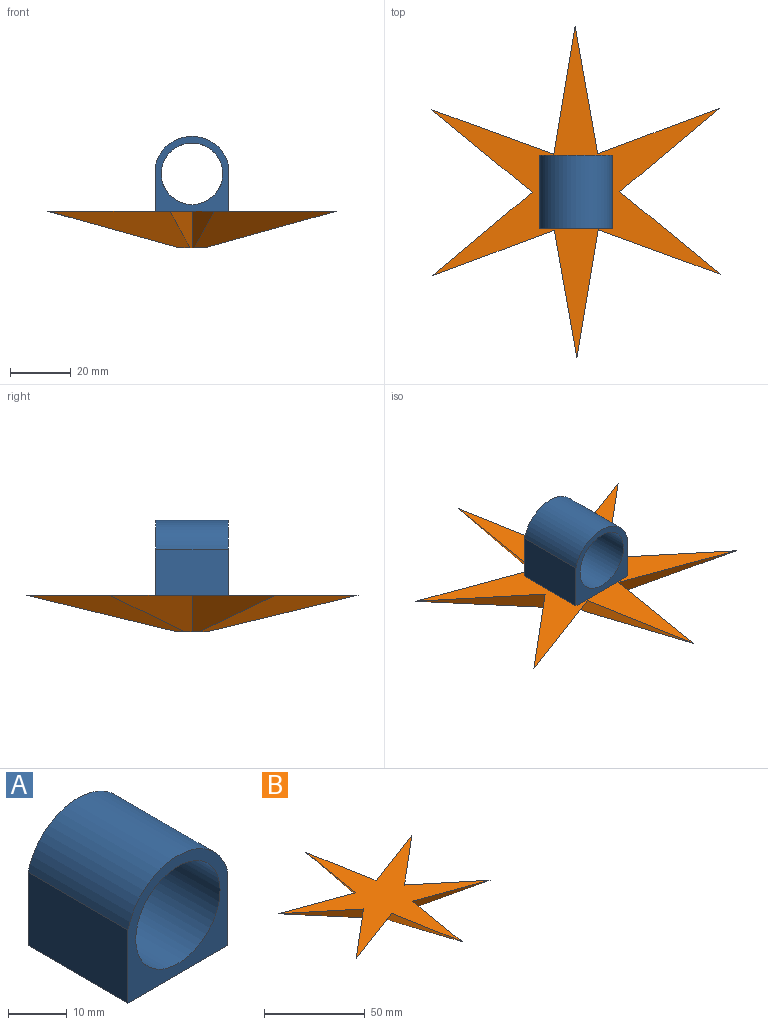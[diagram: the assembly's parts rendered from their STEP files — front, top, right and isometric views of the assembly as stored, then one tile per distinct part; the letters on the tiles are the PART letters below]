
ASSEMBLY  parts=2 mates=1
PART A: 7 faces, bbox 24x24x24.7 mm
  f0: plane 24x15.2mm, normal (-1,0,0), area 364.8mm2, adj f2,f3,f4,f5
  f1: plane 24x15.2mm, normal (1,0,0), area 364.8mm2, adj f2,f3,f4,f5
  f2: plane 24.67x24mm, normal (0,1,0), area 211.6mm2, adj f0,f1,f4,f5,f6
  f3: plane 24.67x24mm, normal (0,-1,0), area 211.6mm2, adj f0,f1,f4,f5,f6
  f4: plane 24x24mm, normal (0,0,-1), area 576mm2, adj f0,f1,f2,f3
  f5: cylinder r=12.34mm len=24mm, axis (0,-1,0), area 791.5mm2, adj f0,f1,f2,f3
  f6: cylinder r=10.13mm len=24mm, axis (0,-1,0), area 1527.2mm2, adj f2,f3
PART B: 14 faces, bbox 95x109.3x12 mm
  f0: plane 53.54x12mm, normal (-0.81,0.13,-0.57), area 342mm2, adj f1,f11,f12,f13
  f1: plane 46.79x25.96mm, normal (0.28,0.77,-0.57), area 341.6mm2, adj f0,f2,f12,f13
  f2: plane 46.16x27.19mm, normal (-0.52,-0.63,-0.57), area 342mm2, adj f1,f3,f12,f13
  f3: plane 45.88x27.54mm, normal (-0.53,0.63,-0.57), area 341.6mm2, adj f2,f4,f12,f13
  f4: plane 46.57x26.41mm, normal (0.29,-0.77,-0.57), area 342mm2, adj f3,f5,f12,f13
  f5: plane 53.5x12mm, normal (-0.81,-0.14,-0.57), area 341.6mm2, adj f4,f6,f12,f13
  f6: plane 53.54x12mm, normal (0.81,-0.13,-0.57), area 342mm2, adj f5,f7,f12,f13
  f7: plane 46.79x25.96mm, normal (-0.28,-0.77,-0.57), area 341.6mm2, adj f6,f8,f12,f13
  f8: plane 46.16x27.19mm, normal (0.52,0.63,-0.57), area 342mm2, adj f7,f9,f12,f13
  f9: plane 45.88x27.54mm, normal (0.53,-0.63,-0.57), area 341.6mm2, adj f8,f10,f12,f13
  f10: plane 46.57x26.41mm, normal (-0.29,0.77,-0.57), area 342mm2, adj f9,f11,f12,f13
  f11: plane 53.5x12mm, normal (0.81,0.14,-0.57), area 341.6mm2, adj f0,f10,f12,f13
  f12: plane 109.34x94.97mm, normal (0,0,1), area 2372.6mm2, adj f0,f1,f2,f3,f4,f5,f6,f7
  f13: plane 10x8.71mm, normal (0,0,-1), area 19.8mm2, adj f0,f1,f2,f3,f4,f5,f6,f7
PLACE A t=(24.23,20.22,0.83)mm
PLACE B t=(34.86,12.13,-11.17)mm
MATE revolute B.f12 <-> A.f4  axis (0,0,1) through (34.86,12.13,0.83)mm
